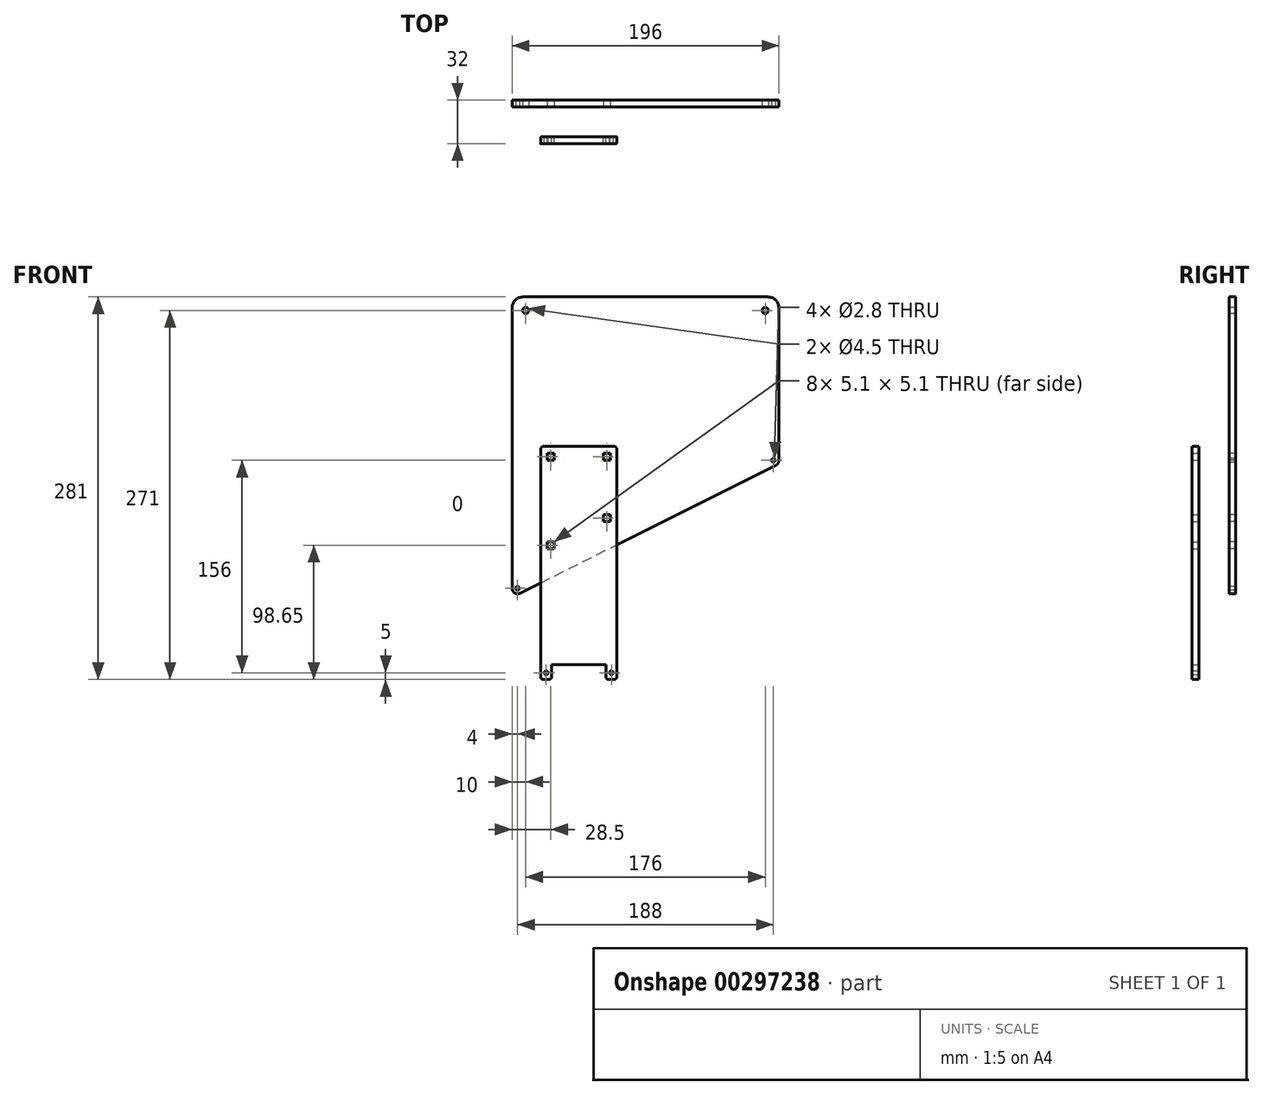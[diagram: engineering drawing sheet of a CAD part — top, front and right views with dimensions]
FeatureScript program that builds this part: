
annotation { "Feature Type Name" : "Feature", "Feature Type Description" : "" }
export const myFeature = defineFeature(function(context is Context, id is Id, definition is map)
    precondition{}
    {
        {
            var Q0;
            Q0=qCreatedBy(makeId("Front.planeOp"),FACE);
            var sketch = newSketch(context, id + "F0", { "sketchPlane" : qUnion([Q0])});
            skArc(sketch, "E0", {"start": v(144.79, 157.42) * mm, "mid": v(146.4, 158.9) * mm, "end": v(147, 161) * mm});
            skLineSegment(sketch, "E1", {"start": v(-49, 67) * mm, "end": v(-49, 273) * mm});
            skCircle(sketch, "E2", {"center": v(-45, 67) * mm, "radius": 1.4 * mm});
            skCircle(sketch, "E3", {"center": v(143, 161) * mm, "radius": 1.4 * mm});
            skArc(sketch, "E4", {"start": v(-49, 67) * mm, "mid": v(-47.1, 63.6) * mm, "end": v(-43.21, 63.42) * mm});
            skLineSegment(sketch, "E5", {"start": v(-43.21, 63.42) * mm, "end": v(144.79, 157.42) * mm});
            skLineSegment(sketch, "E6", {"start": v(147, 273) * mm, "end": v(147, 161) * mm});
            skLineSegment(sketch, "E7.bottom", {"start": v(-23.05, 166.2) * mm, "end": v(-17.95, 166.2) * mm});
            skLineSegment(sketch, "E7.top", {"start": v(-23.05, 161.1) * mm, "end": v(-17.95, 161.1) * mm});
            skLineSegment(sketch, "E7.left", {"start": v(-23.05, 166.2) * mm, "end": v(-23.05, 161.1) * mm});
            skLineSegment(sketch, "E7.right", {"start": v(-17.95, 166.2) * mm, "end": v(-17.95, 161.1) * mm});
            skLineSegment(sketch, "E8.bottom", {"start": v(17.95, 166.2) * mm, "end": v(23.05, 166.2) * mm});
            skLineSegment(sketch, "E8.top", {"start": v(17.95, 161.1) * mm, "end": v(23.05, 161.1) * mm});
            skLineSegment(sketch, "E8.left", {"start": v(17.95, 166.2) * mm, "end": v(17.95, 161.1) * mm});
            skLineSegment(sketch, "E8.right", {"start": v(23.05, 166.2) * mm, "end": v(23.05, 161.1) * mm});
            skLineSegment(sketch, "E9.bottom", {"start": v(-23.05, 101.2) * mm, "end": v(-17.95, 101.2) * mm});
            skLineSegment(sketch, "E9.top", {"start": v(-23.05, 96.1) * mm, "end": v(-17.95, 96.1) * mm});
            skLineSegment(sketch, "E9.left", {"start": v(-23.05, 101.2) * mm, "end": v(-23.05, 96.1) * mm});
            skLineSegment(sketch, "E9.right", {"start": v(-17.95, 101.2) * mm, "end": v(-17.95, 96.1) * mm});
            skLineSegment(sketch, "E10.bottom", {"start": v(23.05, 121.2) * mm, "end": v(17.95, 121.2) * mm});
            skLineSegment(sketch, "E10.top", {"start": v(23.05, 116.1) * mm, "end": v(17.95, 116.1) * mm});
            skLineSegment(sketch, "E10.left", {"start": v(23.05, 121.2) * mm, "end": v(23.05, 116.1) * mm});
            skLineSegment(sketch, "E10.right", {"start": v(17.95, 121.2) * mm, "end": v(17.95, 116.1) * mm});
            skPoint(sketch, "E11", {"position": v(-20.5, 166.2) * mm});
            skPoint(sketch, "E12", {"position": v(20.5, 166.2) * mm});
            skPoint(sketch, "E13", {"position": v(23.05, 163.65) * mm});
            skPoint(sketch, "E14", {"position": v(-23.05, 163.65) * mm});
            skPoint(sketch, "E15", {"position": v(-23.05, 98.65) * mm});
            skPoint(sketch, "E16", {"position": v(17.95, 118.65) * mm});
            skPoint(sketch, "E17.middle.positionSnap0", {"position": v(23.05, 118.65) * mm});
            skPoint(sketch, "E17.centerSnap0", {"position": v(23.05, 118.65) * mm});
            skPoint(sketch, "E18", {"position": v(0, 0) * mm});
            skLineSegment(sketch, "E19", {"start": v(-41, 281) * mm, "end": v(139, 281) * mm});
            skArc(sketch, "E20.filletArc", {"start": v(-41, 281) * mm, "mid": v(-46.66, 278.66) * mm, "end": v(-49, 273) * mm});
            skArc(sketch, "E21.filletArc", {"start": v(147, 273) * mm, "mid": v(144.66, 278.66) * mm, "end": v(139, 281) * mm});
            skCircle(sketch, "E22", {"center": v(-39, 271) * mm, "radius": 2.25 * mm});
            skCircle(sketch, "E23", {"center": v(137, 271) * mm, "radius": 2.25 * mm});
            skSolve(sketch);
        }
        {
            var Q0;
            Q0=qCreatedBy(makeId("Front.planeOp"),FACE);
            cPlane(context, id + "F1", {"entities" : qUnion([Q0]), "cplaneType" : CPlaneType.OFFSET, "offset" : (17 + 5) * mm, "width" : 150 * mm, "height" : 150 * mm});
        }
        {
            var Q0;
            Q0=qCreatedBy(id+"F1.planeOp",FACE);
            var sketch = newSketch(context, id + "F2", { "sketchPlane" : qUnion([Q0])});
            skPoint(sketch, "E24", {"position": v(0, 0) * mm});
            skCircle(sketch, "E25", {"center": v(-24, 5) * mm, "radius": 1.4 * mm});
            skCircle(sketch, "E26", {"center": v(24, 5) * mm, "radius": 1.4 * mm});
            skLineSegment(sketch, "E27", {"start": v(-26, 0) * mm, "end": v(-22, 0) * mm});
            skLineSegment(sketch, "E28.trimOffspring", {"start": v(22, 0) * mm, "end": v(26, 0) * mm});
            skLineSegment(sketch, "E29.top", {"start": v(-20, 11) * mm, "end": v(20, 11) * mm});
            skLineSegment(sketch, "E29.left", {"start": v(-20, 2) * mm, "end": v(-20, 11) * mm});
            skLineSegment(sketch, "E29.right", {"start": v(20, 2) * mm, "end": v(20, 11) * mm});
            skPoint(sketch, "E29.middle", {"position": v(0, 5.5) * mm});
            skLineSegment(sketch, "E30", {"start": v(-28, 2) * mm, "end": v(-28, 169.15) * mm});
            skLineSegment(sketch, "E31", {"start": v(-26, 171.15) * mm, "end": v(26, 171.15) * mm});
            skLineSegment(sketch, "E32", {"start": v(28, 169.15) * mm, "end": v(28, 2) * mm});
            skLineSegment(sketch, "E33.bottom", {"start": v(-23.05, 166.2) * mm, "end": v(-17.95, 166.2) * mm});
            skLineSegment(sketch, "E33.top", {"start": v(-23.05, 161.1) * mm, "end": v(-17.95, 161.1) * mm});
            skLineSegment(sketch, "E33.left", {"start": v(-23.05, 166.2) * mm, "end": v(-23.05, 161.1) * mm});
            skLineSegment(sketch, "E33.right", {"start": v(-17.95, 166.2) * mm, "end": v(-17.95, 161.1) * mm});
            skLineSegment(sketch, "E34.bottom", {"start": v(17.95, 166.2) * mm, "end": v(23.05, 166.2) * mm});
            skLineSegment(sketch, "E34.top", {"start": v(17.95, 161.1) * mm, "end": v(23.05, 161.1) * mm});
            skLineSegment(sketch, "E34.left", {"start": v(17.95, 166.2) * mm, "end": v(17.95, 161.1) * mm});
            skLineSegment(sketch, "E34.right", {"start": v(23.05, 166.2) * mm, "end": v(23.05, 161.1) * mm});
            skLineSegment(sketch, "E35.bottom", {"start": v(-23.05, 101.2) * mm, "end": v(-17.95, 101.2) * mm});
            skLineSegment(sketch, "E35.top", {"start": v(-23.05, 96.1) * mm, "end": v(-17.95, 96.1) * mm});
            skLineSegment(sketch, "E35.left", {"start": v(-23.05, 101.2) * mm, "end": v(-23.05, 96.1) * mm});
            skLineSegment(sketch, "E35.right", {"start": v(-17.95, 101.2) * mm, "end": v(-17.95, 96.1) * mm});
            skLineSegment(sketch, "E36.bottom", {"start": v(23.05, 121.2) * mm, "end": v(17.95, 121.2) * mm});
            skLineSegment(sketch, "E36.top", {"start": v(23.05, 116.1) * mm, "end": v(17.95, 116.1) * mm});
            skLineSegment(sketch, "E36.left", {"start": v(23.05, 121.2) * mm, "end": v(23.05, 116.1) * mm});
            skLineSegment(sketch, "E36.right", {"start": v(17.95, 121.2) * mm, "end": v(17.95, 116.1) * mm});
            skPoint(sketch, "E37.visualSharp", {"position": v(-28, 0) * mm});
            skArc(sketch, "E37.filletArc", {"start": v(-28, 2) * mm, "mid": v(-27.41, 0.59) * mm, "end": v(-26, 0) * mm});
            skPoint(sketch, "E38.visualSharp", {"position": v(-20, 0) * mm});
            skArc(sketch, "E38.filletArc", {"start": v(-22, 0) * mm, "mid": v(-20.59, 0.59) * mm, "end": v(-20, 2) * mm});
            skPoint(sketch, "E39.visualSharp", {"position": v(20, 0) * mm});
            skArc(sketch, "E39.filletArc", {"start": v(20, 2) * mm, "mid": v(20.59, 0.59) * mm, "end": v(22, 0) * mm});
            skPoint(sketch, "E40.visualSharp", {"position": v(28, 0) * mm});
            skArc(sketch, "E40.filletArc", {"start": v(26, 0) * mm, "mid": v(27.41, 0.59) * mm, "end": v(28, 2) * mm});
            skPoint(sketch, "E41.visualSharp", {"position": v(-28, 171.15) * mm});
            skArc(sketch, "E41.filletArc", {"start": v(-26, 171.15) * mm, "mid": v(-27.41, 170.56) * mm, "end": v(-28, 169.15) * mm});
            skPoint(sketch, "E42.visualSharp", {"position": v(28, 171.15) * mm});
            skArc(sketch, "E42.filletArc", {"start": v(28, 169.15) * mm, "mid": v(27.41, 170.56) * mm, "end": v(26, 171.15) * mm});
            skPoint(sketch, "E43", {"position": v(-20.5, 166.2) * mm});
            skPoint(sketch, "E44", {"position": v(20.5, 166.2) * mm});
            skPoint(sketch, "E45", {"position": v(23.05, 163.65) * mm});
            skPoint(sketch, "E46", {"position": v(-23.05, 163.65) * mm});
            skPoint(sketch, "E47", {"position": v(-23.05, 98.65) * mm});
            skPoint(sketch, "E48", {"position": v(17.95, 118.65) * mm});
            skLineSegment(sketch, "E49", {"start": v(38, 171.15) * mm, "end": v(38, 166.15) * mm});
            skLineSegment(sketch, "E50.bottom", {"start": v(38, 161.15) * mm, "end": v(33, 161.15) * mm});
            skLineSegment(sketch, "E50.top", {"start": v(38, 166.15) * mm, "end": v(33, 166.15) * mm});
            skLineSegment(sketch, "E50.right", {"start": v(33, 161.15) * mm, "end": v(33, 166.15) * mm});
            skPoint(sketch, "E50.middle", {"position": v(35.5, 163.65) * mm});
            skLineSegment(sketch, "E51.bottom", {"start": v(38, 116.15) * mm, "end": v(33, 116.15) * mm});
            skLineSegment(sketch, "E51.top", {"start": v(38, 121.15) * mm, "end": v(33, 121.15) * mm});
            skLineSegment(sketch, "E51.right", {"start": v(33, 116.15) * mm, "end": v(33, 121.15) * mm});
            skPoint(sketch, "E51.middle", {"position": v(35.5, 118.65) * mm});
            skPoint(sketch, "E51.middle.positionSnap0", {"position": v(23.05, 118.65) * mm});
            skPoint(sketch, "E51.centerSnap0", {"position": v(23.05, 118.65) * mm});
            skLineSegment(sketch, "E52.bottom", {"start": v(-40, 166.15) * mm, "end": v(-35, 166.15) * mm});
            skLineSegment(sketch, "E52.top", {"start": v(-40, 161.15) * mm, "end": v(-35, 161.15) * mm});
            skLineSegment(sketch, "E52.right", {"start": v(-35, 166.15) * mm, "end": v(-35, 161.15) * mm});
            skPoint(sketch, "E52.middle", {"position": v(-37.5, 163.65) * mm});
            skLineSegment(sketch, "E53.bottom", {"start": v(-40, 101.15) * mm, "end": v(-35, 101.15) * mm});
            skLineSegment(sketch, "E53.top", {"start": v(-40, 96.15) * mm, "end": v(-35, 96.15) * mm});
            skLineSegment(sketch, "E53.right", {"start": v(-35, 101.15) * mm, "end": v(-35, 96.15) * mm});
            skPoint(sketch, "E53.middle", {"position": v(-37.5, 98.65) * mm});
            skLineSegment(sketch, "E54.trimOffspring", {"start": v(38, 161.15) * mm, "end": v(38, 121.15) * mm});
            skLineSegment(sketch, "E55.trimOffspring", {"start": v(38, 116.15) * mm, "end": v(38, 111.15) * mm});
            skLineSegment(sketch, "E56", {"start": v(38, 171.15) * mm, "end": v(59, 171.15) * mm});
            skLineSegment(sketch, "E57", {"start": v(59, 171.15) * mm, "end": v(59, 166.15) * mm});
            skLineSegment(sketch, "E58", {"start": v(59, 166.15) * mm, "end": v(64, 166.15) * mm});
            skLineSegment(sketch, "E59", {"start": v(64, 166.15) * mm, "end": v(64, 161.15) * mm});
            skLineSegment(sketch, "E60", {"start": v(64, 161.15) * mm, "end": v(59, 161.15) * mm});
            skLineSegment(sketch, "E61", {"start": v(59, 161.15) * mm, "end": v(59, 121.15) * mm});
            skLineSegment(sketch, "E62", {"start": v(59, 121.15) * mm, "end": v(64, 121.15) * mm});
            skLineSegment(sketch, "E63", {"start": v(64, 121.15) * mm, "end": v(64, 116.15) * mm});
            skLineSegment(sketch, "E64", {"start": v(64, 116.15) * mm, "end": v(59, 116.15) * mm});
            skLineSegment(sketch, "E65", {"start": v(59, 116.15) * mm, "end": v(59, 111.15) * mm});
            skLineSegment(sketch, "E66", {"start": v(59, 111.15) * mm, "end": v(38, 111.15) * mm});
            skLineSegment(sketch, "E67.trimOffspring", {"start": v(-40, 161.15) * mm, "end": v(-40, 101.15) * mm});
            skPoint(sketch, "E68.start.orphan", {"position": v(-40, 171.15) * mm});
            skLineSegment(sketch, "E69.trimOffspring", {"start": v(-40, 96.15) * mm, "end": v(-40, 91.15) * mm});
            skLineSegment(sketch, "E70", {"start": v(-40, 166.15) * mm, "end": v(-40, 171.15) * mm});
            skLineSegment(sketch, "E71", {"start": v(-40, 171.15) * mm, "end": v(-61, 171.15) * mm});
            skLineSegment(sketch, "E72", {"start": v(-61, 171.15) * mm, "end": v(-61, 166.15) * mm});
            skLineSegment(sketch, "E73", {"start": v(-61, 166.15) * mm, "end": v(-66, 166.15) * mm});
            skLineSegment(sketch, "E74", {"start": v(-66, 166.15) * mm, "end": v(-66, 161.15) * mm});
            skPoint(sketch, "E74.endSnap0", {"position": v(-37.5, 161.15) * mm});
            skLineSegment(sketch, "E75", {"start": v(-66, 161.15) * mm, "end": v(-61, 161.15) * mm});
            skLineSegment(sketch, "E76", {"start": v(-61, 161.15) * mm, "end": v(-61, 101.15) * mm});
            skLineSegment(sketch, "E77", {"start": v(-61, 101.15) * mm, "end": v(-66, 101.15) * mm});
            skLineSegment(sketch, "E78", {"start": v(-66, 101.15) * mm, "end": v(-66, 96.15) * mm});
            skLineSegment(sketch, "E79", {"start": v(-66, 96.15) * mm, "end": v(-61, 96.15) * mm});
            skLineSegment(sketch, "E80", {"start": v(-61, 96.15) * mm, "end": v(-61, 91.15) * mm});
            skLineSegment(sketch, "E81", {"start": v(-61, 91.15) * mm, "end": v(-40, 91.15) * mm});
            skSolve(sketch);
        }
        {
            var Q0;
            Q0=makeQuery(id+"F0.imprint","IMPRINT",FACE,{"disambiguationData":[TD([[makeQuery(id+"F0.imprint","IMPRINT",EDGE,{"derivedFrom":sQuery(id+"F0.wireOp",EDGE,"E0")}),1.0]])]});
            extrude(context, id + "F3", {"entities" : qUnion([Q0]), "oppositeDirection" : true, "depth" : 5 * mm});
        }
        {
            var Q0;
            Q0=makeQuery(id+"F2.imprint","IMPRINT",FACE,{"disambiguationData":[TD([[makeQuery(id+"F2.imprint","IMPRINT",EDGE,{"derivedFrom":sQuery(id+"F2.wireOp",EDGE,"E25")}),-1.0]])]});
            extrude(context, id + "F4", {"entities" : qUnion([Q0]), "depth" : 5 * mm});
        }
    });
